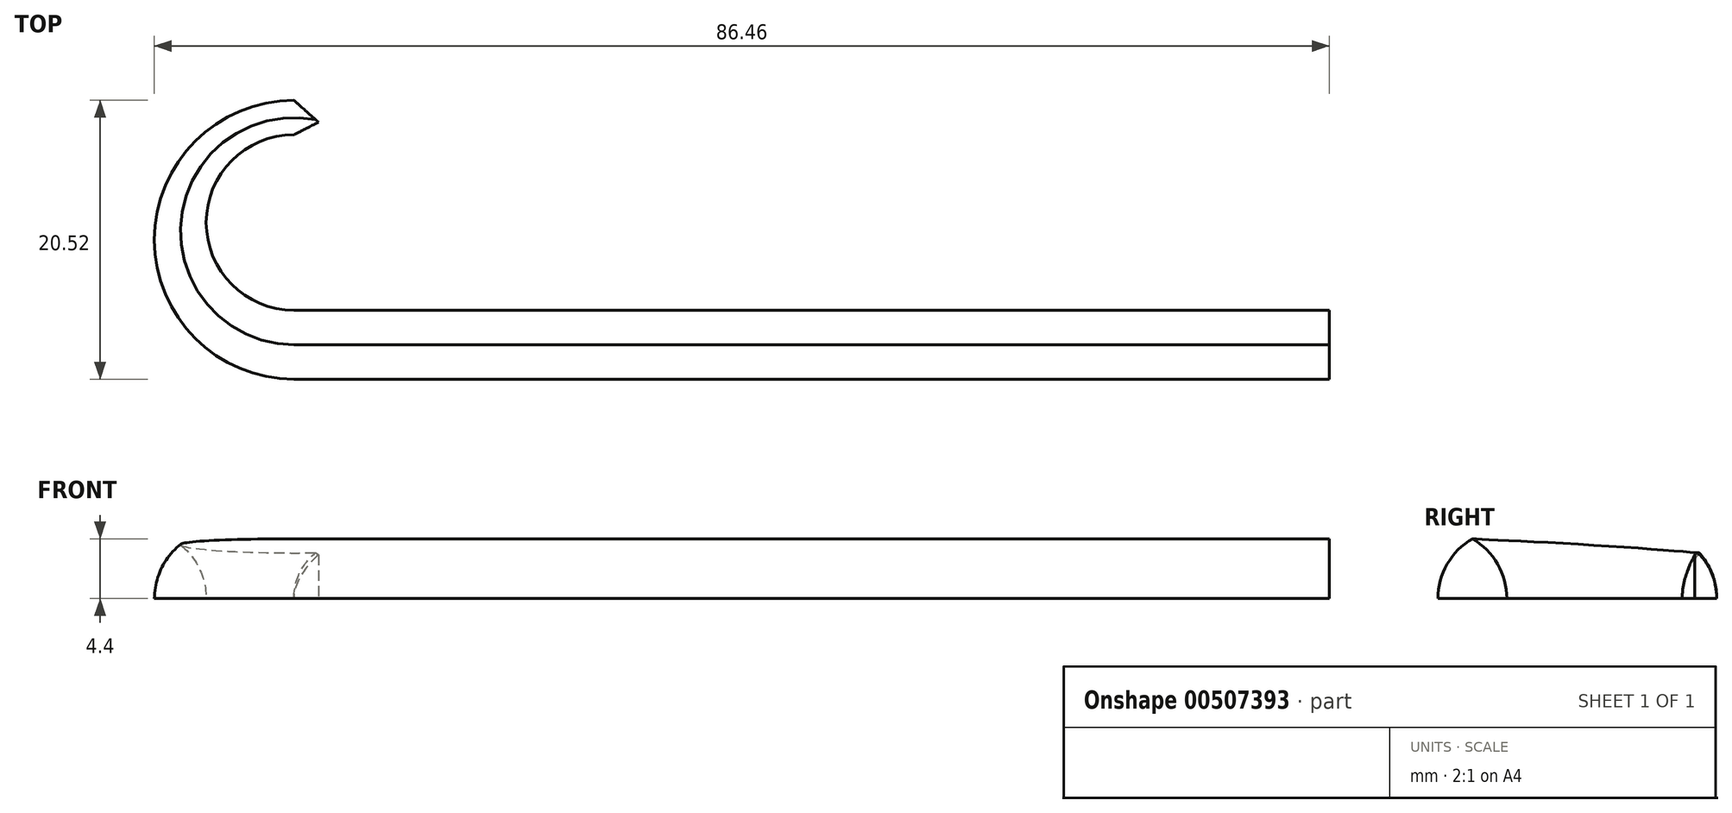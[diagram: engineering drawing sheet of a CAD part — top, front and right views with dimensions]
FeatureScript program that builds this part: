
annotation { "Feature Type Name" : "Feature", "Feature Type Description" : "" }
export const myFeature = defineFeature(function(context is Context, id is Id, definition is map)
    precondition{}
    {
        {
            var Q0;
            Q0=qCreatedBy(makeId("Top.planeOp"),FACE);
            var sketch = newSketch(context, id + "F0", { "sketchPlane" : qUnion([Q0])});
            skLineSegment(sketch, "E0.bottom", {"start": v(-38.1, 2.54) * mm, "end": v(38.1, 2.54) * mm});
            skLineSegment(sketch, "E0.top", {"start": v(-38.1, -2.54) * mm, "end": v(38.1, -2.54) * mm});
            skLineSegment(sketch, "E0.left", {"start": v(-38.1, 2.54) * mm, "end": v(-38.1, -2.54) * mm});
            skLineSegment(sketch, "E0.right", {"start": v(38.1, 2.54) * mm, "end": v(38.1, -2.54) * mm});
            skPoint(sketch, "E0.middle", {"position": v(0, 0) * mm});
            skArc(sketch, "E1", {"start": v(-38.1, 15.44) * mm, "mid": v(-44.55, 9) * mm, "end": v(-38.1, 2.54) * mm});
            skArc(sketch, "E2", {"start": v(-38.1, 17.98) * mm, "mid": v(-48.36, 7.72) * mm, "end": v(-38.1, -2.54) * mm});
            skLineSegment(sketch, "E3", {"start": v(-38.1, 15.44) * mm, "end": v(-36.29, 16.38) * mm});
            skLineSegment(sketch, "E4", {"start": v(-36.29, 16.38) * mm, "end": v(-38.1, 17.98) * mm});
            skSolve(sketch);
        }
        {
            var Q0;
            Q0=makeQuery(id+"F0.imprint","IMPRINT",FACE,{"disambiguationData":[TD([[makeQuery(id+"F0.imprint","IMPRINT",EDGE,{"derivedFrom":sQuery(id+"F0.wireOp",EDGE,"E0.left")}),-1.0]])]});
            extrude(context, id + "F1", {"entities" : qUnion([Q0]), "depth" : 5.08 * mm});
        }
        {
            var Q0;
            Q0=makeQuery(id+"F0.imprint","IMPRINT",FACE,{"disambiguationData":[TD([[makeQuery(id+"F0.imprint","IMPRINT",EDGE,{"derivedFrom":sQuery(id+"F0.wireOp",EDGE,"E0.bottom")}),-1.0]])]});
            extrude(context, id + "F2", {"entities" : qUnion([Q0]), "operationType" : NewBodyOperationType.ADD, "depth" : 5.08 * mm});
        }
        {
            var Q0;
            Q0=makeQuery(id+"F2.opExtrude","CAP_EDGE",EDGE,{"disambiguationData":[OSD([sQuery(id+"F0.wireOp",EDGE,"E0.bottom")])],"isStart":false});
            var Q1;
            Q1=makeQuery(id+"F2.opExtrude","CAP_EDGE",EDGE,{"disambiguationData":[OSD([sQuery(id+"F0.wireOp",EDGE,"E0.top")])],"isStart":false});
            fillet(context, id + "F3", {"entities" : qUnion([Q0, Q1]), "radius" : 5.08 * mm, "tangentPropagation" : true, "allowEdgeOverflow" : false});
        }
    });
